FCSTD DOCUMENT  (FreeCAD 0.20R29410 (Git))
Label: LoGoRenewed10_15_22
License: All rights reserved
LicenseURL: http://en.wikipedia.org/wiki/All_rights_reserved
objects: Part::Feature×3, Part::Box×2, Mesh::Feature×1, Part::MultiFuse×1, Part::Cut×1, Part::FeaturePython×1
note: 8 computed .brp shape members not serialized (recipe doc carries the construction recipe); baked Part::Feature solids carry a one-line shape summary decoded from their .brp

FEATURE [Mesh::Feature] logo3mmWidth
FEATURE [Part::Feature] logo3mmWidth001
  Placement = pos=(18.4,14,-4) rot=(0,0,1;0rad)
  shape: bbox 30 x 22.21 x 4.944 mm, 7244 faces, 0 solids (baked)
FEATURE [Part::Box] Box  label="Cube"
  AttacherType = Attacher::AttachEngine3D
  Height = 1.5
  Length = 36
  Width = 29
FEATURE [Part::Box] Box001  label="Cube001"
  AttacherType = Attacher::AttachEngine3D
  Height = 5.5
  Length = 36
  Placement = pos=(0,0,3.6) rot=(0,0,1;0rad)
  Width = 29
FEATURE [Part::Feature] logo3mmWidth001_solid  label="logo3mmWidth001 (Solid)"
  shape: bbox 30 x 22.21 x 4.944 mm, 7244 faces (baked)
FEATURE [Part::MultiFuse] Fusion
  Shapes = -> [Box,logo3mmWidth001_solid]
FEATURE [Part::Cut] Cut  label="logo"
  Base = -> Fusion
  Tool = -> Box001
FEATURE [Part::FeaturePython] Clone  label="Cut001"  # Draft clone (typed FeaturePython)
  AttacherType = Attacher::AttachEngine3D
  Fuse = false
  Objects = -> [Cut]
  Placement = pos=(0.92,0.65,0) rot=(0,0,1;0rad)
  Scale = (0.98,0.95,0.95)
FEATURE [Part::Feature] Clone001  label="95"
  Placement = pos=(0.92,0.65,0) rot=(0,0,1;0rad)
  shape: bbox 34.2 x 27.55 x 3.42 mm, 3615 faces (baked)
